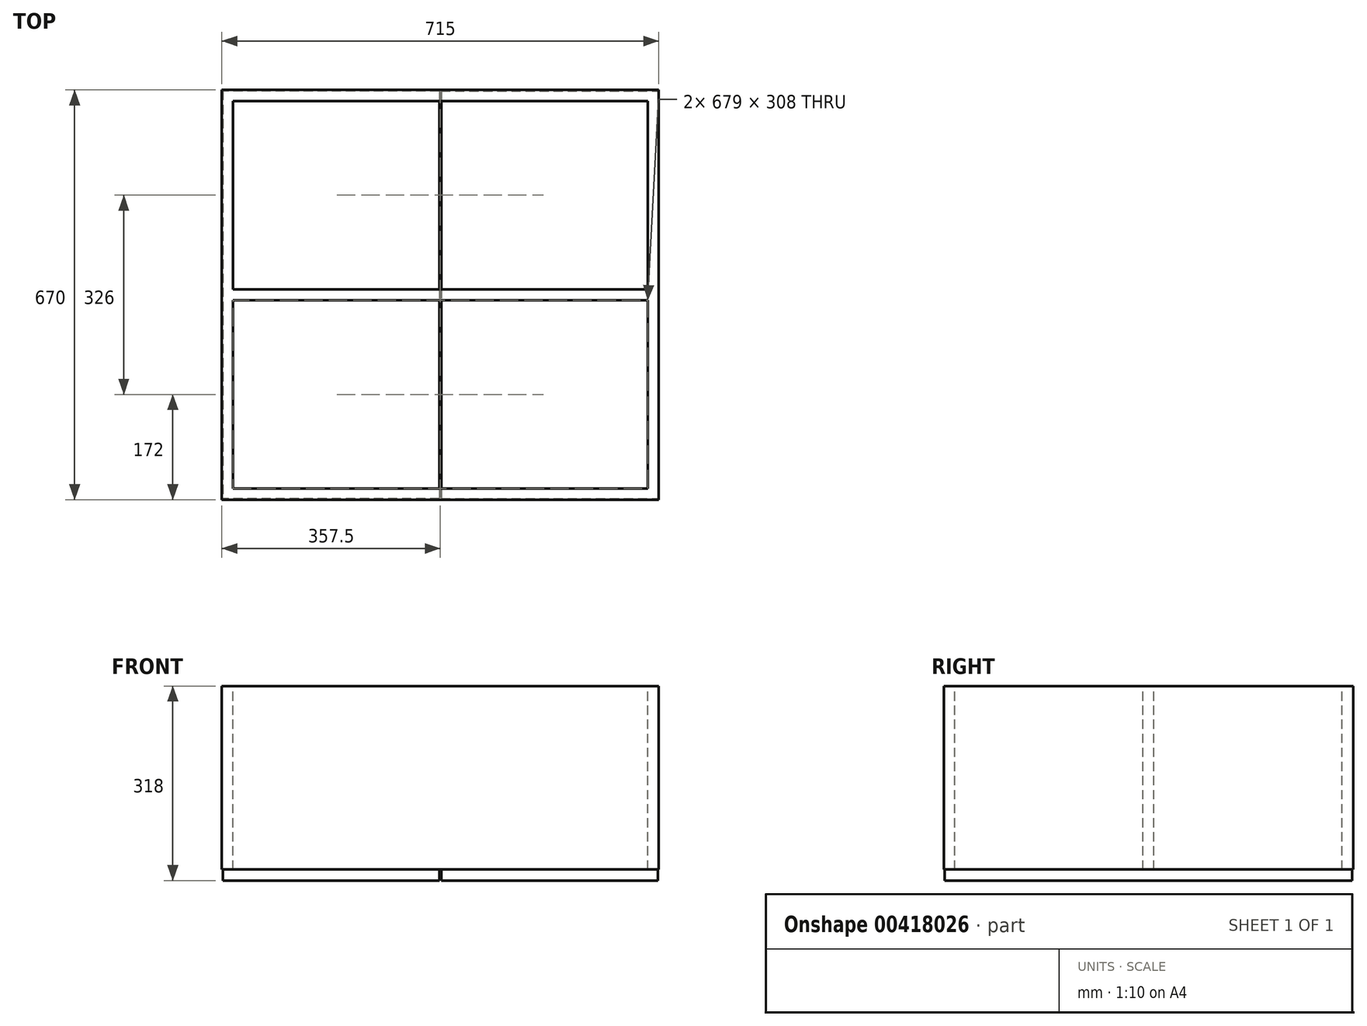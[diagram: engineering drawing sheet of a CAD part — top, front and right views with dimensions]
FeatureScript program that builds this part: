
annotation { "Feature Type Name" : "Feature", "Feature Type Description" : "" }
export const myFeature = defineFeature(function(context is Context, id is Id, definition is map)
    precondition{}
    {
        {
            var Q0;
            Q0=qCreatedBy(makeId("Front.planeOp"),FACE);
            var sketch = newSketch(context, id + "F0", { "sketchPlane" : qUnion([Q0])});
            skLineSegment(sketch, "E0.bottom", {"start": v(-339.5, -150) * mm, "end": v(339.5, -150) * mm});
            skLineSegment(sketch, "E0.top", {"start": v(-339.5, 150) * mm, "end": v(339.5, 150) * mm});
            skLineSegment(sketch, "E0.left", {"start": v(-339.5, -150) * mm, "end": v(-339.5, 150) * mm});
            skLineSegment(sketch, "E0.right", {"start": v(339.5, -150) * mm, "end": v(339.5, 150) * mm});
            skPoint(sketch, "E0.middle", {"position": v(0, 0) * mm});
            skLineSegment(sketch, "E1.bottom", {"start": v(-339.5, -150) * mm, "end": v(-357.5, -150) * mm});
            skLineSegment(sketch, "E1.top", {"start": v(-339.5, 150) * mm, "end": v(-357.5, 150) * mm});
            skLineSegment(sketch, "E1.right", {"start": v(-357.5, -150) * mm, "end": v(-357.5, 150) * mm});
            skLineSegment(sketch, "E2.bottom", {"start": v(339.5, -150) * mm, "end": v(357.5, -150) * mm});
            skLineSegment(sketch, "E2.top", {"start": v(339.5, 150) * mm, "end": v(357.5, 150) * mm});
            skLineSegment(sketch, "E2.right", {"start": v(357.5, -150) * mm, "end": v(357.5, 150) * mm});
            skLineSegment(sketch, "E3", {"start": v(0, 0) * mm, "end": v(0, -229) * mm, "construction": true});
            skLineSegment(sketch, "E4.bottom", {"start": v(356, -168) * mm, "end": v(-356, -168) * mm});
            skLineSegment(sketch, "E4.top", {"start": v(356, -150) * mm, "end": v(-356, -150) * mm});
            skLineSegment(sketch, "E4.left", {"start": v(356, -168) * mm, "end": v(356, -150) * mm});
            skLineSegment(sketch, "E4.right", {"start": v(-356, -168) * mm, "end": v(-356, -150) * mm});
            skPoint(sketch, "E4.middle", {"position": v(0, -159) * mm});
            skLineSegment(sketch, "E5", {"start": v(1.5, -150) * mm, "end": v(1.5, -168) * mm});
            skLineSegment(sketch, "E6", {"start": v(-1.5, -150) * mm, "end": v(-1.5, -168) * mm});
            skSolve(sketch);
        }
        {
            var Q0;
            {var subQ1=sQuery(id+"F0.wireOp",EDGE,"E1.bottom");Q0=makeQuery(id+"F0.imprint","IMPRINT",FACE,{"disambiguationData":[TD([[makeQuery(id+"F0.imprint","IMPRINT",EDGE,{"derivedFrom":subQ1}),-1.0]])]});}
            var Q1;
            {var subQ1=sQuery(id+"F0.wireOp",EDGE,"E2.bottom");Q1=makeQuery(id+"F0.imprint","IMPRINT",FACE,{"disambiguationData":[TD([[makeQuery(id+"F0.imprint","IMPRINT",EDGE,{"derivedFrom":subQ1}),1.0]])]});}
            extrude(context, id + "F1", {"entities" : qUnion([Q0, Q1]), "depth" : 670 * mm});
        }
        {
            var Q0;
            Q0=makeQuery(id+"F0.imprint","IMPRINT",FACE,{"disambiguationData":[TD([[makeQuery(id+"F0.imprint","IMPRINT",EDGE,{"derivedFrom":sQuery(id+"F0.wireOp",EDGE,"E0.top")}),-1.0]])]});
            cPlane(context, id + "F2", {"entities" : qUnion([Q0]), "cplaneType" : CPlaneType.OFFSET, "offset" : 670 * mm, "width" : 150 * mm, "height" : 150 * mm});
        }
        {
            var Q0;
            Q0=qCreatedBy(id+"F2.planeOp",FACE);
            var sketch = newSketch(context, id + "F3", { "sketchPlane" : qUnion([Q0])});
            skLineSegment(sketch, "E7.bottom", {"start": v(-339.5, -150) * mm, "end": v(339.5, -150) * mm});
            skLineSegment(sketch, "E7.top", {"start": v(-339.5, 150) * mm, "end": v(339.5, 150) * mm});
            skLineSegment(sketch, "E7.left", {"start": v(-339.5, -150) * mm, "end": v(-339.5, 150) * mm});
            skLineSegment(sketch, "E7.right", {"start": v(339.5, -150) * mm, "end": v(339.5, 150) * mm});
            skPoint(sketch, "E7.middle", {"position": v(0, 0) * mm});
            skLineSegment(sketch, "E8.bottom", {"start": v(-339.5, -150) * mm, "end": v(-357.5, -150) * mm});
            skLineSegment(sketch, "E8.top", {"start": v(-339.5, 150) * mm, "end": v(-357.5, 150) * mm});
            skLineSegment(sketch, "E8.right", {"start": v(-357.5, -150) * mm, "end": v(-357.5, 150) * mm});
            skLineSegment(sketch, "E9.bottom", {"start": v(339.5, -150) * mm, "end": v(357.5, -150) * mm});
            skLineSegment(sketch, "E9.top", {"start": v(339.5, 150) * mm, "end": v(357.5, 150) * mm});
            skLineSegment(sketch, "E9.right", {"start": v(357.5, -150) * mm, "end": v(357.5, 150) * mm});
            skLineSegment(sketch, "E10", {"start": v(0, 0) * mm, "end": v(0, -61.92) * mm, "construction": true});
            skLineSegment(sketch, "E11.bottom", {"start": v(356, -168) * mm, "end": v(-356, -168) * mm});
            skLineSegment(sketch, "E11.top", {"start": v(356, -150) * mm, "end": v(-356, -150) * mm});
            skLineSegment(sketch, "E11.left", {"start": v(356, -168) * mm, "end": v(356, -150) * mm});
            skLineSegment(sketch, "E11.right", {"start": v(-356, -168) * mm, "end": v(-356, -150) * mm});
            skPoint(sketch, "E11.middle", {"position": v(0, -159) * mm});
            skSolve(sketch);
        }
        {
            var Q0;
            Q0=makeQuery(id+"F3.imprint","IMPRINT",FACE,{"disambiguationData":[TD([[makeQuery(id+"F3.imprint","IMPRINT",EDGE,{"derivedFrom":sQuery(id+"F3.wireOp",EDGE,"E7.top")}),-1.0]])]});
            extrude(context, id + "F4", {"entities" : qUnion([Q0]), "oppositeDirection" : true, "depth" : 18 * mm});
        }
        {
            var Q0;
            Q0=makeQuery(id+"F0.imprint","IMPRINT",FACE,{"disambiguationData":[TD([[makeQuery(id+"F0.imprint","IMPRINT",EDGE,{"derivedFrom":sQuery(id+"F0.wireOp",EDGE,"E0.top")}),-1.0]])]});
            extrude(context, id + "F5", {"entities" : qUnion([Q0]), "depth" : 18 * mm});
        }
        {
            var Q0;
            Q0=makeQuery(id+"F0.imprint","IMPRINT",FACE,{"disambiguationData":[TD([[makeQuery(id+"F0.imprint","IMPRINT",EDGE,{"derivedFrom":sQuery(id+"F0.wireOp",EDGE,"E0.top")}),-1.0]])]});
            cPlane(context, id + "F6", {"entities" : qUnion([Q0]), "cplaneType" : CPlaneType.OFFSET, "offset" : 335 * mm, "width" : 150 * mm, "height" : 150 * mm});
        }
        {
            var Q0;
            Q0=qCreatedBy(id+"F6.planeOp",FACE);
            var sketch = newSketch(context, id + "F7", { "sketchPlane" : qUnion([Q0])});
            skLineSegment(sketch, "E12.bottom", {"start": v(-339.5, -150) * mm, "end": v(339.5, -150) * mm});
            skLineSegment(sketch, "E12.top", {"start": v(-339.5, 150) * mm, "end": v(339.5, 150) * mm});
            skLineSegment(sketch, "E12.left", {"start": v(-339.5, -150) * mm, "end": v(-339.5, 150) * mm});
            skLineSegment(sketch, "E12.right", {"start": v(339.5, -150) * mm, "end": v(339.5, 150) * mm});
            skPoint(sketch, "E12.middle", {"position": v(0, 0) * mm});
            skLineSegment(sketch, "E13.bottom", {"start": v(-339.5, -150) * mm, "end": v(-357.5, -150) * mm});
            skLineSegment(sketch, "E13.top", {"start": v(-339.5, 150) * mm, "end": v(-357.5, 150) * mm});
            skLineSegment(sketch, "E13.right", {"start": v(-357.5, -150) * mm, "end": v(-357.5, 150) * mm});
            skLineSegment(sketch, "E14.bottom", {"start": v(339.5, -150) * mm, "end": v(357.5, -150) * mm});
            skLineSegment(sketch, "E14.top", {"start": v(339.5, 150) * mm, "end": v(357.5, 150) * mm});
            skLineSegment(sketch, "E14.right", {"start": v(357.5, -150) * mm, "end": v(357.5, 150) * mm});
            skLineSegment(sketch, "E15", {"start": v(0, 0) * mm, "end": v(0, -59.6) * mm, "construction": true});
            skLineSegment(sketch, "E16.bottom", {"start": v(356, -168) * mm, "end": v(-356, -168) * mm});
            skLineSegment(sketch, "E16.top", {"start": v(356, -150) * mm, "end": v(-356, -150) * mm});
            skLineSegment(sketch, "E16.left", {"start": v(356, -168) * mm, "end": v(356, -150) * mm});
            skLineSegment(sketch, "E16.right", {"start": v(-356, -168) * mm, "end": v(-356, -150) * mm});
            skPoint(sketch, "E16.middle", {"position": v(0, -159) * mm});
            skSolve(sketch);
        }
        {
            var Q0;
            Q0=makeQuery(id+"F7.imprint","IMPRINT",FACE,{"disambiguationData":[TD([[makeQuery(id+"F7.imprint","IMPRINT",EDGE,{"derivedFrom":sQuery(id+"F7.wireOp",EDGE,"E12.top")}),-1.0]])]});
            extrude(context, id + "F8", {"entities" : qUnion([Q0]), "endBound" : BoundingType.SYMMETRIC, "depth" : 18 * mm});
        }
        {
            var Q0;
            Q0=makeQuery(id+"F1.opExtrude","SWEPT_BODY",BODY,{"disambiguationData":[OSD([sQuery(id+"F0.wireOp",EDGE,"E1.bottom"),sQuery(id+"F0.wireOp",EDGE,"E1.top"),sQuery(id+"F0.wireOp",EDGE,"E0.left"),sQuery(id+"F0.wireOp",EDGE,"E1.right"),sQuery(id+"F0.wireOp",EDGE,"E4.top")])]});
            var Q1;
            Q1=makeQuery(id+"F1.opExtrude","SWEPT_BODY",BODY,{"disambiguationData":[OSD([sQuery(id+"F0.wireOp",EDGE,"E2.bottom"),sQuery(id+"F0.wireOp",EDGE,"E2.top"),sQuery(id+"F0.wireOp",EDGE,"E0.right"),sQuery(id+"F0.wireOp",EDGE,"E2.right"),sQuery(id+"F0.wireOp",EDGE,"E4.top")])]});
            var Q2;
            Q2=makeQuery(id+"F4.opExtrude","SWEPT_BODY",BODY,{"disambiguationData":[OSD([sQuery(id+"F3.wireOp",EDGE,"E7.top"),sQuery(id+"F3.wireOp",EDGE,"E7.left"),sQuery(id+"F3.wireOp",EDGE,"E7.right"),sQuery(id+"F3.wireOp",EDGE,"E11.top")])]});
            var Q3;
            Q3=makeQuery(id+"F5.opExtrude","SWEPT_BODY",BODY,{"disambiguationData":[OSD([sQuery(id+"F0.wireOp",EDGE,"E0.top"),sQuery(id+"F0.wireOp",EDGE,"E0.left"),sQuery(id+"F0.wireOp",EDGE,"E0.right"),sQuery(id+"F0.wireOp",EDGE,"E4.top")])]});
            var Q4;
            Q4=makeQuery(id+"F8.opExtrude","SWEPT_BODY",BODY,{"disambiguationData":[OSD([sQuery(id+"F7.wireOp",EDGE,"E12.top"),sQuery(id+"F7.wireOp",EDGE,"E12.left"),sQuery(id+"F7.wireOp",EDGE,"E12.right"),sQuery(id+"F7.wireOp",EDGE,"E16.top")])]});
            booleanBodies(context, id + "F9", {"operationType" : BooleanOperationType.UNION, "tools" : qUnion([Q0, Q1, Q2, Q3, Q4])});
        }
        {
            var Q0;
            {var subQ0=sQuery(id+"F0.wireOp",EDGE,"E4.top");Q0=makeQuery(id+"F9.opBoolean","MERGE",FACE,{"derivedFrom":[makeQuery(id+"F1.opExtrude","CAP_FACE",FACE,{"disambiguationData":[OSD([sQuery(id+"F0.wireOp",EDGE,"E1.bottom"),sQuery(id+"F0.wireOp",EDGE,"E1.top"),sQuery(id+"F0.wireOp",EDGE,"E0.left"),sQuery(id+"F0.wireOp",EDGE,"E1.right"),subQ0])],"isStart":false}),makeQuery(id+"F1.opExtrude","CAP_FACE",FACE,{"disambiguationData":[OSD([sQuery(id+"F0.wireOp",EDGE,"E2.bottom"),sQuery(id+"F0.wireOp",EDGE,"E2.top"),sQuery(id+"F0.wireOp",EDGE,"E0.right"),sQuery(id+"F0.wireOp",EDGE,"E2.right"),subQ0])],"isStart":false}),makeQuery(id+"F4.opExtrude","CAP_FACE",FACE,{"disambiguationData":[OSD([sQuery(id+"F3.wireOp",EDGE,"E7.top"),sQuery(id+"F3.wireOp",EDGE,"E7.left"),sQuery(id+"F3.wireOp",EDGE,"E7.right"),sQuery(id+"F3.wireOp",EDGE,"E11.top")])],"isStart":true})]});}
            cPlane(context, id + "F10", {"entities" : qUnion([Q0]), "cplaneType" : CPlaneType.OFFSET, "offset" : 1.5 * mm, "oppositeDirection" : true, "width" : 150 * mm, "height" : 150 * mm});
        }
        {
            var Q0;
            Q0=qCreatedBy(id+"F10.planeOp",FACE);
            var sketch = newSketch(context, id + "F11", { "sketchPlane" : qUnion([Q0])});
            skPoint(sketch, "E17.middle", {"position": v(0, 0) * mm});
            skLineSegment(sketch, "E18.bottom", {"start": v(-339.5, -150) * mm, "end": v(339.5, -150) * mm});
            skLineSegment(sketch, "E18.top", {"start": v(-339.5, 150) * mm, "end": v(339.5, 150) * mm});
            skLineSegment(sketch, "E18.left", {"start": v(-339.5, -150) * mm, "end": v(-339.5, 150) * mm});
            skLineSegment(sketch, "E18.right", {"start": v(339.5, -150) * mm, "end": v(339.5, 150) * mm});
            skLineSegment(sketch, "E19.bottom", {"start": v(-339.5, -150) * mm, "end": v(-357.5, -150) * mm});
            skLineSegment(sketch, "E19.top", {"start": v(-339.5, 150) * mm, "end": v(-357.5, 150) * mm});
            skLineSegment(sketch, "E19.right", {"start": v(-357.5, -150) * mm, "end": v(-357.5, 150) * mm});
            skLineSegment(sketch, "E20.bottom", {"start": v(339.5, -150) * mm, "end": v(357.5, -150) * mm});
            skLineSegment(sketch, "E20.top", {"start": v(339.5, 150) * mm, "end": v(357.5, 150) * mm});
            skLineSegment(sketch, "E20.right", {"start": v(357.5, -150) * mm, "end": v(357.5, 150) * mm});
            skLineSegment(sketch, "E21", {"start": v(0, 9.2) * mm, "end": v(0, 0) * mm, "construction": true});
            skLineSegment(sketch, "E22.bottom", {"start": v(356, -168) * mm, "end": v(-356, -168) * mm});
            skLineSegment(sketch, "E22.top", {"start": v(356, -150) * mm, "end": v(-356, -150) * mm});
            skLineSegment(sketch, "E22.left", {"start": v(356, -168) * mm, "end": v(356, -150) * mm});
            skLineSegment(sketch, "E22.right", {"start": v(-356, -168) * mm, "end": v(-356, -150) * mm});
            skPoint(sketch, "E22.middle", {"position": v(0, -159) * mm});
            skLineSegment(sketch, "E23", {"start": v(1.5, -150) * mm, "end": v(1.5, -168) * mm});
            skLineSegment(sketch, "E24", {"start": v(-1.5, -150) * mm, "end": v(-1.5, -168) * mm});
            skSolve(sketch);
        }
        {
            var Q0;
            {var subQ0=sQuery(id+"F11.wireOp",EDGE,"E22.right");Q0=makeQuery(id+"F11.imprint","IMPRINT",FACE,{"disambiguationData":[TD([[makeQuery(id+"F11.imprint","IMPRINT",EDGE,{"derivedFrom":subQ0}),-1.0]])]});}
            var Q1;
            {var subQ3=sQuery(id+"F11.wireOp",EDGE,"E22.left");Q1=makeQuery(id+"F11.imprint","IMPRINT",FACE,{"disambiguationData":[TD([[makeQuery(id+"F11.imprint","IMPRINT",EDGE,{"derivedFrom":subQ3}),1.0]])]});}
            extrude(context, id + "F12", {"entities" : qUnion([Q0, Q1]), "oppositeDirection" : true, "depth" : 667 * mm});
        }
    });
